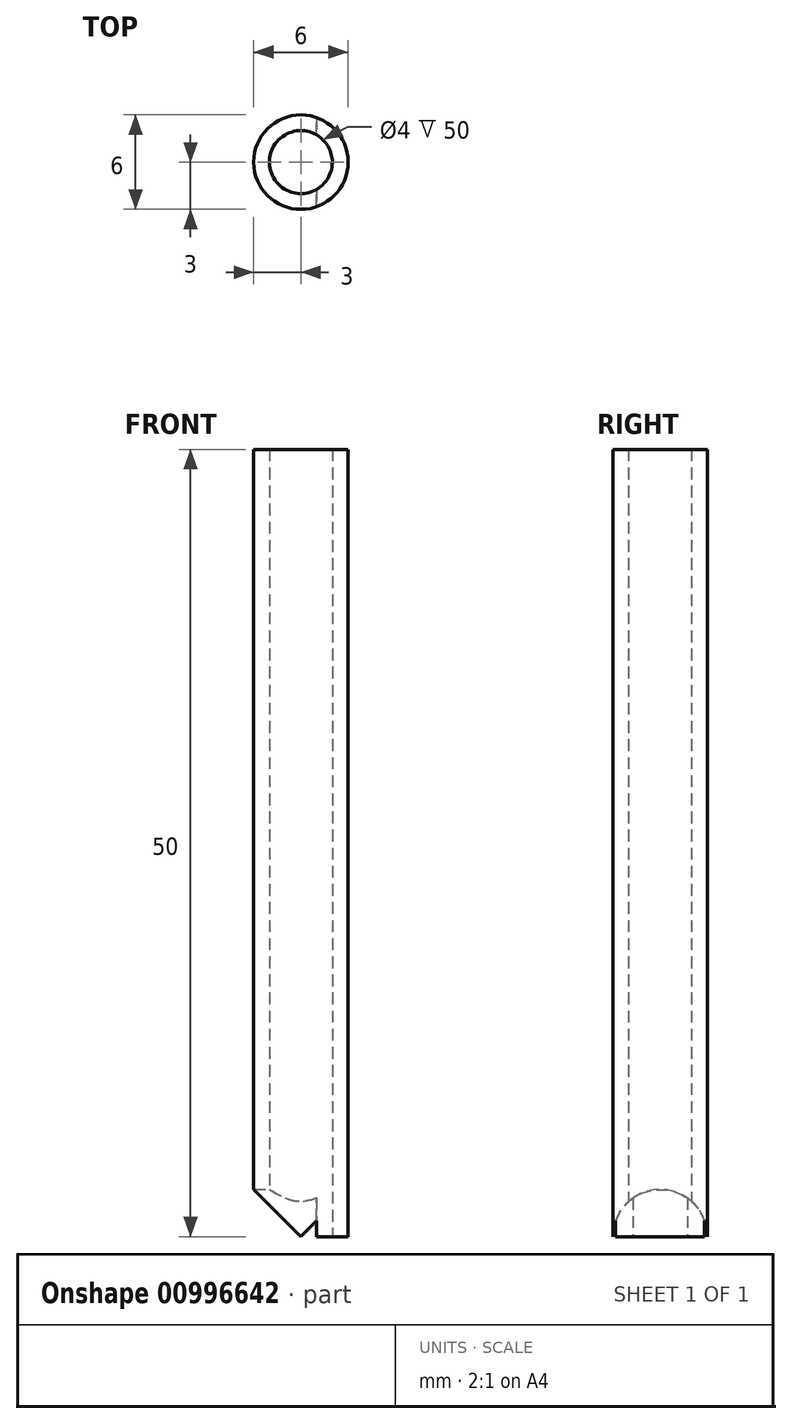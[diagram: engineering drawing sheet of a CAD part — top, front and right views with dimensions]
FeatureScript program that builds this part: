
annotation { "Feature Type Name" : "Feature", "Feature Type Description" : "" }
export const myFeature = defineFeature(function(context is Context, id is Id, definition is map)
    precondition{}
    {
        {
            var Q0;
            Q0=qCreatedBy(makeId("Top.planeOp"),FACE);
            var sketch = newSketch(context, id + "F0", { "sketchPlane" : qUnion([Q0])});
            skCircle(sketch, "E0", {"center": v(0, 0) * mm, "radius": 2 * mm});
            skCircle(sketch, "E1", {"center": v(0, 0) * mm, "radius": 3 * mm});
            skSolve(sketch);
        }
        {
            var Q0;
            Q0=makeQuery(id+"F0.imprint","IMPRINT",FACE,{"disambiguationData":[TD([[makeQuery(id+"F0.imprint","IMPRINT",EDGE,{"derivedFrom":sQuery(id+"F0.wireOp",EDGE,"E0")}),-1.0]])]});
            extrude(context, id + "F1", {"entities" : qUnion([Q0]), "depth" : 50 * mm, "offsetDistance" : 25 * mm});
        }
        {
            var Q0;
            Q0=qCreatedBy(makeId("Right.planeOp"),FACE);
            var sketch = newSketch(context, id + "F2", { "sketchPlane" : qUnion([Q0])});
            skCircle(sketch, "E2", {"center": v(0, 0) * mm, "radius": 3 * mm});
            skSolve(sketch);
        }
        {
            var Q0;
            Q0=makeQuery(id+"F2.imprint","IMPRINT",FACE,{"disambiguationData":[TD([[makeQuery(id+"F2.imprint","IMPRINT",EDGE,{"derivedFrom":sQuery(id+"F2.wireOp",EDGE,"E2")}),1.0]])]});
            extrude(context, id + "F3", {"entities" : qUnion([Q0]), "operationType" : NewBodyOperationType.REMOVE, "oppositeDirection" : true, "depth" : 25 * mm, "offsetDistance" : 25 * mm, "hasSecondDirection" : true, "secondDirectionOppositeDirection" : false, "secondDirectionDepth" : 1 * mm});
        }
    });
